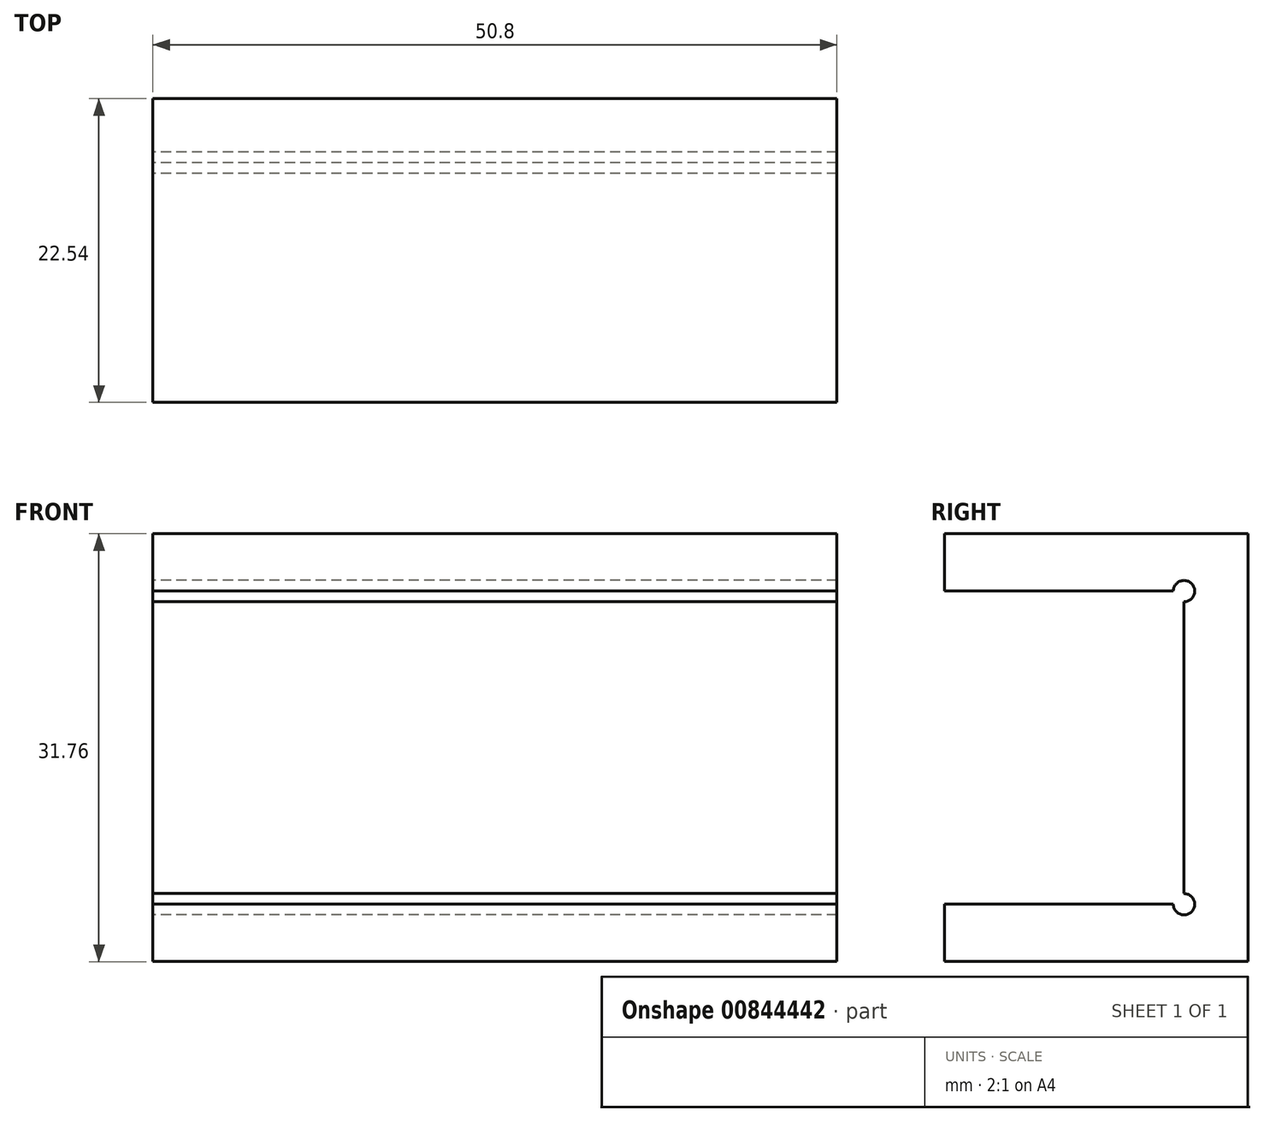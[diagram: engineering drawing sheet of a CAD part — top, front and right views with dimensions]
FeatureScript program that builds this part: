
annotation { "Feature Type Name" : "Feature", "Feature Type Description" : "" }
export const myFeature = defineFeature(function(context is Context, id is Id, definition is map)
    precondition{}
    {
        {
            var Q0;
            Q0=qCreatedBy(makeId("Front.planeOp"),FACE);
            var sketch = newSketch(context, id + "F0", { "sketchPlane" : qUnion([Q0])});
            skLineSegment(sketch, "E0.bottom", {"start": v(-25.4, -15.88) * mm, "end": v(25.4, -15.88) * mm});
            skLineSegment(sketch, "E0.top", {"start": v(-25.4, 15.88) * mm, "end": v(25.4, 15.88) * mm});
            skLineSegment(sketch, "E0.left", {"start": v(-25.4, -15.88) * mm, "end": v(-25.4, 15.88) * mm});
            skLineSegment(sketch, "E0.right", {"start": v(25.4, -15.88) * mm, "end": v(25.4, 15.88) * mm});
            skPoint(sketch, "E0.middle", {"position": v(0, 0) * mm});
            skLineSegment(sketch, "E1.bottom", {"start": v(-25.4, 11.62) * mm, "end": v(25.4, 11.62) * mm});
            skLineSegment(sketch, "E1.top", {"start": v(-25.4, -11.62) * mm, "end": v(25.4, -11.62) * mm});
            skLineSegment(sketch, "E1.left", {"start": v(-25.4, 11.62) * mm, "end": v(-25.4, -11.62) * mm});
            skLineSegment(sketch, "E1.right", {"start": v(25.4, 11.62) * mm, "end": v(25.4, -11.62) * mm});
            skSolve(sketch);
        }
        {
            var Q0;
            {var subQ0=sQuery(id+"F0.wireOp",EDGE,"E0.top");Q0=makeQuery(id+"F0.imprint","IMPRINT",FACE,{"disambiguationData":[TD([[makeQuery(id+"F0.imprint","IMPRINT",EDGE,{"derivedFrom":subQ0}),-1.0]])]});}
            var Q1;
            Q1=makeQuery(id+"F0.imprint","IMPRINT",FACE,{"disambiguationData":[TD([[makeQuery(id+"F0.imprint","IMPRINT",EDGE,{"derivedFrom":sQuery(id+"F0.wireOp",EDGE,"E1.bottom")}),-1.0]])]});
            var Q2;
            {var subQ0=sQuery(id+"F0.wireOp",EDGE,"E0.bottom");Q2=makeQuery(id+"F0.imprint","IMPRINT",FACE,{"disambiguationData":[TD([[makeQuery(id+"F0.imprint","IMPRINT",EDGE,{"derivedFrom":subQ0}),1.0]])]});}
            extrude(context, id + "F1", {"entities" : qUnion([Q0, Q1, Q2]), "oppositeDirection" : true, "depth" : 4.76 * mm, "offsetDistance" : 25.4 * mm});
        }
        {
            var Q0;
            {var subQ0=sQuery(id+"F0.wireOp",EDGE,"E0.top");Q0=makeQuery(id+"F0.imprint","IMPRINT",FACE,{"disambiguationData":[TD([[makeQuery(id+"F0.imprint","IMPRINT",EDGE,{"derivedFrom":subQ0}),-1.0]])]});}
            var Q1;
            {var subQ0=sQuery(id+"F0.wireOp",EDGE,"E0.bottom");Q1=makeQuery(id+"F0.imprint","IMPRINT",FACE,{"disambiguationData":[TD([[makeQuery(id+"F0.imprint","IMPRINT",EDGE,{"derivedFrom":subQ0}),1.0]])]});}
            extrude(context, id + "F2", {"entities" : qUnion([Q0, Q1]), "operationType" : NewBodyOperationType.ADD, "depth" : 17.78 * mm, "offsetDistance" : 25.4 * mm});
        }
        {
            var Q0;
            {var subQ0=sQuery(id+"F0.wireOp",EDGE,"E0.left");var subQ1=sQuery(id+"F0.wireOp",EDGE,"E1.left");Q0=makeQuery(id+"F2.boolean.opBoolean","MERGE",FACE,{"derivedFrom":[makeQuery(id+"F1.opExtrude","SWEPT_FACE",FACE,{"disambiguationData":[OSD([subQ0,subQ1])]}),makeQuery(id+"F2.opExtrude","SWEPT_FACE",FACE,{"disambiguationData":[OSD([subQ0]),TDD([makeQuery(id+"F0.imprint","IMPRINT",EDGE,{"disambiguationData":[TD([[makeQuery(id+"F0.imprint","INTERSECT",VERTEX,{"derivedFrom":[sQuery(id+"F0.wireOp",EDGE,"E0.bottom"),subQ0]}),-1.0]])],"derivedFrom":subQ0})])]}),makeQuery(id+"F2.opExtrude","SWEPT_FACE",FACE,{"disambiguationData":[OSD([subQ0]),TDD([makeQuery(id+"F0.imprint","IMPRINT",EDGE,{"disambiguationData":[TD([[makeQuery(id+"F0.imprint","INTERSECT",VERTEX,{"derivedFrom":[sQuery(id+"F0.wireOp",EDGE,"E0.top"),subQ0]}),1.0]])],"derivedFrom":subQ0})])]})]});}
            var sketch = newSketch(context, id + "F3", { "sketchPlane" : qUnion([Q0])});
            skCircle(sketch, "E2", {"center": v(0, 11.62) * mm, "radius": 0.8 * mm});
            skCircle(sketch, "E3", {"center": v(0, -11.62) * mm, "radius": 0.8 * mm});
            skSolve(sketch);
        }
        {
            var Q0;
            {var subQ0=sQuery(id+"F3.wireOp",EDGE,"E2");var subQ1=sQuery(id+"F0.wireOp",EDGE,"E1.left");var subQ2=sQuery(id+"F0.wireOp",EDGE,"E0.left");var subQ5=makeQuery(id+"F1.opExtrude","CAP_EDGE",EDGE,{"disambiguationData":[OSD([subQ2,subQ1])],"isStart":true});var subQ6=makeQuery(id+"F3.imprint","INTERSECT",VERTEX,{"derivedFrom":[subQ5,subQ0]});Q0=makeQuery(id+"F3.imprint","IMPRINT",FACE,{"disambiguationData":[TD([[makeQuery(id+"F3.imprint","IMPRINT",EDGE,{"disambiguationData":[TD([[subQ6,1.0]])],"derivedFrom":subQ0}),1.0]])]});}
            var Q1;
            {var subQ0=sQuery(id+"F3.wireOp",EDGE,"E3");var subQ1=sQuery(id+"F0.wireOp",EDGE,"E1.left");var subQ2=sQuery(id+"F0.wireOp",EDGE,"E0.left");var subQ5=makeQuery(id+"F1.opExtrude","CAP_EDGE",EDGE,{"disambiguationData":[OSD([subQ2,subQ1])],"isStart":true});var subQ6=makeQuery(id+"F3.imprint","INTERSECT",VERTEX,{"derivedFrom":[subQ5,subQ0]});Q1=makeQuery(id+"F3.imprint","IMPRINT",FACE,{"disambiguationData":[TD([[makeQuery(id+"F3.imprint","IMPRINT",EDGE,{"disambiguationData":[TD([[subQ6,-1.0]])],"derivedFrom":subQ0}),1.0]])]});}
            extrude(context, id + "F4", {"entities" : qUnion([Q0, Q1]), "operationType" : NewBodyOperationType.REMOVE, "endBound" : BoundingType.THROUGH_ALL, "oppositeDirection" : true, "depth" : 25.4 * mm, "offsetDistance" : 25.4 * mm});
        }
    });
